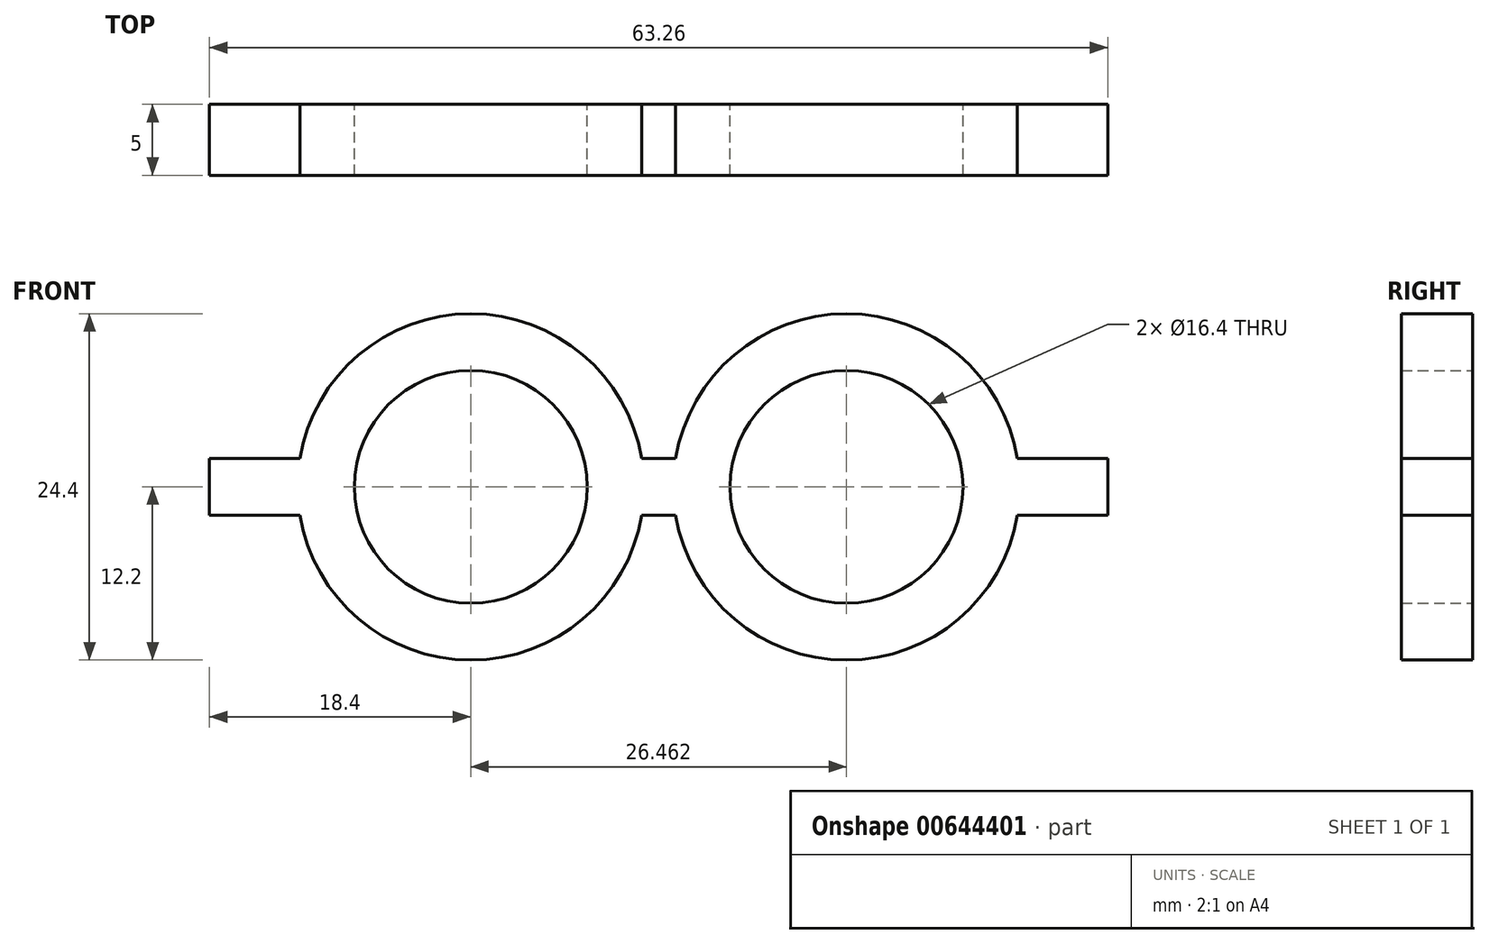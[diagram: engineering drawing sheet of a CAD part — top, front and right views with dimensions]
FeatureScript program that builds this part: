
annotation { "Feature Type Name" : "Feature", "Feature Type Description" : "" }
export const myFeature = defineFeature(function(context is Context, id is Id, definition is map)
    precondition{}
    {
        {
            var Q0;
            Q0=qCreatedBy(makeId("Front.planeOp"),FACE);
            var sketch = newSketch(context, id + "F0", { "sketchPlane" : qUnion([Q0])});
            skCircle(sketch, "E0", {"center": v(0, 0) * mm, "radius": 8.2 * mm});
            skArc(sketch, "E1.0", {"start": v(-12.03, -2) * mm, "mid": v(0, -12.2) * mm, "end": v(12.03, -2) * mm});
            skCircle(sketch, "E2", {"center": v(26.46, 0) * mm, "radius": 8.2 * mm});
            skArc(sketch, "E3.0", {"start": v(38.5, 2) * mm, "mid": v(26.46, 12.2) * mm, "end": v(14.43, 2) * mm});
            skLineSegment(sketch, "E4.bottom", {"start": v(12.03, 2) * mm, "end": v(14.43, 2) * mm});
            skLineSegment(sketch, "E4.top", {"start": v(12.03, -2) * mm, "end": v(14.43, -2) * mm});
            skPoint(sketch, "E4.middle", {"position": v(13.23, 0) * mm});
            skLineSegment(sketch, "E5.bottom", {"start": v(-18.4, -2) * mm, "end": v(-12.03, -2) * mm});
            skLineSegment(sketch, "E5.top", {"start": v(-18.4, 2) * mm, "end": v(-12.03, 2) * mm});
            skLineSegment(sketch, "E5.left", {"start": v(-18.4, -2) * mm, "end": v(-18.4, 2) * mm});
            skPoint(sketch, "E5.middle", {"position": v(-9.2, 0) * mm});
            skLineSegment(sketch, "E6.bottom", {"start": v(44.86, -2) * mm, "end": v(38.5, -2) * mm});
            skLineSegment(sketch, "E6.top", {"start": v(44.86, 2) * mm, "end": v(38.5, 2) * mm});
            skLineSegment(sketch, "E6.left", {"start": v(44.86, -2) * mm, "end": v(44.86, 2) * mm});
            skPoint(sketch, "E6.middle", {"position": v(35.66, 0) * mm});
            skPoint(sketch, "E7.orphan", {"position": v(26.46, -2) * mm});
            skPoint(sketch, "E8.orphan", {"position": v(26.46, 2) * mm});
            skPoint(sketch, "E9.orphan", {"position": v(0, 2) * mm});
            skPoint(sketch, "E5.right.start.orphan", {"position": v(0, -2) * mm});
            skPoint(sketch, "E10.orphan", {"position": v(8.99, 2) * mm});
            skPoint(sketch, "E11.orphan", {"position": v(8.99, -2) * mm});
            skArc(sketch, "E12.trimOffspring", {"start": v(12.03, 2) * mm, "mid": v(0, 12.2) * mm, "end": v(-12.03, 2) * mm});
            skArc(sketch, "E13.trimOffspring", {"start": v(14.43, -2) * mm, "mid": v(26.46, -12.2) * mm, "end": v(38.5, -2) * mm});
            skPoint(sketch, "E14.orphan", {"position": v(17.47, -2) * mm});
            skPoint(sketch, "E15.orphan", {"position": v(17.47, 2) * mm});
            skSolve(sketch);
        }
        {
            var Q0;
            Q0=makeQuery(id+"F0.imprint","IMPRINT",FACE,{"disambiguationData":[TD([[makeQuery(id+"F0.imprint","IMPRINT",EDGE,{"derivedFrom":sQuery(id+"F0.wireOp",EDGE,"E0")}),-1.0]])]});
            extrude(context, id + "F1", {"entities" : qUnion([Q0]), "depth" : 5 * mm, "offsetDistance" : 25 * mm});
        }
    });
